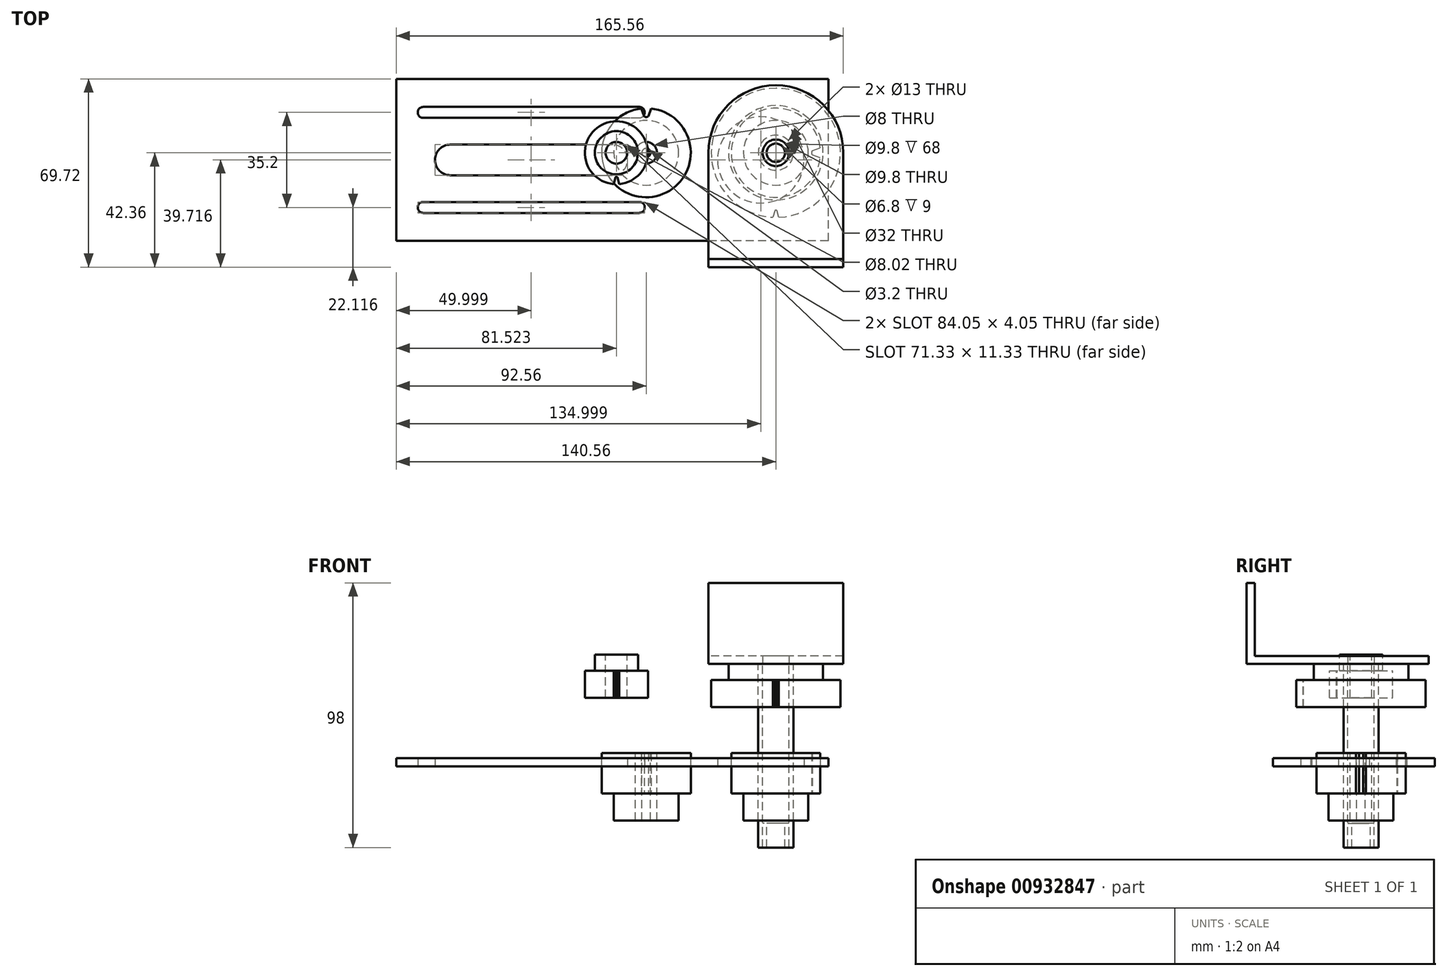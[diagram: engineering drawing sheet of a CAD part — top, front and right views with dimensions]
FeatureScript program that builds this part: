
annotation { "Feature Type Name" : "Feature", "Feature Type Description" : "" }
export const myFeature = defineFeature(function(context is Context, id is Id, definition is map)
    precondition{}
    {
        {
            var Q0;
            Q0=qCreatedBy(makeId("Front.planeOp"),FACE);
            var sketch = newSketch(context, id + "F0", { "sketchPlane" : qUnion([Q0])});
            skLineSegment(sketch, "E0", {"start": v(-76.12, 37.9) * mm, "end": v(-76.12, -21.1) * mm, "construction": true});
            skLineSegment(sketch, "E1", {"start": v(-76.12, -21.1) * mm, "end": v(-81.02, -21.1) * mm, "construction": true});
            skLineSegment(sketch, "E2", {"start": v(-81.02, -21.1) * mm, "end": v(-81.02, -30.1) * mm});
            skLineSegment(sketch, "E3", {"start": v(-81.02, -30.1) * mm, "end": v(-82.62, -30.1) * mm});
            skLineSegment(sketch, "E4", {"start": v(-82.62, -30.1) * mm, "end": v(-82.62, -20.1) * mm});
            skLineSegment(sketch, "E5", {"start": v(-82.62, -20.1) * mm, "end": v(-88.12, -20.1) * mm});
            skLineSegment(sketch, "E6", {"start": v(-88.12, -20.1) * mm, "end": v(-88.12, -10.1) * mm});
            skLineSegment(sketch, "E7", {"start": v(-82.62, -30.1) * mm, "end": v(-82.62, 31.9) * mm});
            skLineSegment(sketch, "E8", {"start": v(-100.04, 31.9) * mm, "end": v(-100.04, 21.9) * mm});
            skLineSegment(sketch, "E9", {"start": v(-139.17, 25.37) * mm, "end": v(-146.83, 25.37) * mm});
            skLineSegment(sketch, "E10", {"start": v(-146.83, 25.37) * mm, "end": v(-146.83, 35.37) * mm});
            skLineSegment(sketch, "E11", {"start": v(-81.02, -21.1) * mm, "end": v(-81.02, 37.9) * mm});
            skLineSegment(sketch, "E12", {"start": v(-81.02, -30.1) * mm, "end": v(-79.52, -30.1) * mm});
            skLineSegment(sketch, "E13", {"start": v(-79.52, -30.1) * mm, "end": v(-79.52, -21.1) * mm});
            skLineSegment(sketch, "E14", {"start": v(-79.52, -21.1) * mm, "end": v(-81.02, -21.1) * mm});
            skLineSegment(sketch, "E15", {"start": v(-82.62, -20.1) * mm, "end": v(-82.62, -30.1) * mm});
            skLineSegment(sketch, "E16", {"start": v(-92.62, -10.1) * mm, "end": v(-92.62, 4.9) * mm});
            skLineSegment(sketch, "E17", {"start": v(-92.62, 4.9) * mm, "end": v(-82.62, 4.9) * mm});
            skLineSegment(sketch, "E18", {"start": v(-124.12, 4.9) * mm, "end": v(-124.12, -20.1) * mm, "construction": true});
            skLineSegment(sketch, "E19", {"start": v(-128.12, -20.1) * mm, "end": v(-128.12, 4.9) * mm});
            skLineSegment(sketch, "E20", {"start": v(-128.12, 4.9) * mm, "end": v(-140.62, 4.9) * mm});
            skLineSegment(sketch, "E21", {"start": v(-140.62, 4.9) * mm, "end": v(-140.62, -10.1) * mm});
            skLineSegment(sketch, "E22", {"start": v(-140.62, -10.1) * mm, "end": v(-136.12, -10.1) * mm});
            skLineSegment(sketch, "E23", {"start": v(-136.12, -10.1) * mm, "end": v(-136.12, -20.1) * mm});
            skLineSegment(sketch, "E24", {"start": v(-136.12, -20.1) * mm, "end": v(-128.12, -20.1) * mm});
            skLineSegment(sketch, "E25", {"start": v(-88.12, -10.1) * mm, "end": v(-92.62, -10.1) * mm});
            skLineSegment(sketch, "E26", {"start": v(-128.12, -20.1) * mm, "end": v(-125.72, -20.1) * mm});
            skLineSegment(sketch, "E27", {"start": v(-125.72, -20.1) * mm, "end": v(-125.72, 4.9) * mm});
            skLineSegment(sketch, "E28", {"start": v(-125.72, -20.1) * mm, "end": v(-124.12, -20.1) * mm, "construction": true});
            skLineSegment(sketch, "E29", {"start": v(-128.12, 4.9) * mm, "end": v(-125.72, 4.9) * mm});
            skLineSegment(sketch, "E30", {"start": v(-125.72, 4.9) * mm, "end": v(-124.12, 4.9) * mm, "construction": true});
            skLineSegment(sketch, "E31", {"start": v(-100.04, 21.9) * mm, "end": v(-82.62, 21.9) * mm});
            skLineSegment(sketch, "E32", {"start": v(-82.62, 31.9) * mm, "end": v(-82.62, 37.9) * mm});
            skLineSegment(sketch, "E33", {"start": v(-82.62, 37.9) * mm, "end": v(-93.62, 37.9) * mm});
            skLineSegment(sketch, "E34", {"start": v(-93.62, 37.9) * mm, "end": v(-93.62, 31.9) * mm});
            skLineSegment(sketch, "E35", {"start": v(-93.62, 31.9) * mm, "end": v(-100.04, 31.9) * mm});
            skLineSegment(sketch, "E36", {"start": v(-139.17, 25.37) * mm, "end": v(-139.17, 41.37) * mm});
            skLineSegment(sketch, "E37", {"start": v(-139.17, 41.37) * mm, "end": v(-143.16, 41.37) * mm});
            skLineSegment(sketch, "E38", {"start": v(-143.16, 41.37) * mm, "end": v(-143.16, 35.37) * mm});
            skLineSegment(sketch, "E39", {"start": v(-146.83, 35.37) * mm, "end": v(-143.16, 35.37) * mm});
            skLineSegment(sketch, "E40", {"start": v(-139.17, 41.37) * mm, "end": v(-135.16, 41.37) * mm, "construction": true});
            skLineSegment(sketch, "E41", {"start": v(-135.16, 41.37) * mm, "end": v(-135.16, 25.37) * mm, "construction": true});
            skLineSegment(sketch, "E42", {"start": v(-135.16, 25.37) * mm, "end": v(-139.17, 25.37) * mm, "construction": true});
            skLineSegment(sketch, "E43", {"start": v(-82.62, 37.9) * mm, "end": v(-81.02, 37.9) * mm});
            skLineSegment(sketch, "E44", {"start": v(-81.02, 37.9) * mm, "end": v(-76.12, 37.9) * mm, "construction": true});
            skSolve(sketch);
        }
        {
            var Q0;
            Q0=qCreatedBy(makeId("Top.planeOp"),FACE);
            var sketch = newSketch(context, id + "F1", { "sketchPlane" : qUnion([Q0])});
            skLineSegment(sketch, "E45.bottom", {"start": v(-56.68, -32.64) * mm, "end": v(-216.68, -32.64) * mm});
            skLineSegment(sketch, "E45.top", {"start": v(-56.68, 27.36) * mm, "end": v(-216.68, 27.36) * mm});
            skLineSegment(sketch, "E45.left", {"start": v(-56.68, -32.64) * mm, "end": v(-56.68, 27.36) * mm});
            skLineSegment(sketch, "E45.right", {"start": v(-216.68, -32.64) * mm, "end": v(-216.68, 27.36) * mm});
            skLineSegment(sketch, "E46.bottom", {"start": v(-126.68, -22.27) * mm, "end": v(-206.68, -22.27) * mm});
            skLineSegment(sketch, "E46.top", {"start": v(-126.68, -18.22) * mm, "end": v(-206.68, -18.22) * mm});
            skLineSegment(sketch, "E46.left", {"start": v(-126.68, -22.27) * mm, "end": v(-126.68, -18.22) * mm});
            skLineSegment(sketch, "E46.right", {"start": v(-206.68, -22.27) * mm, "end": v(-206.68, -18.22) * mm});
            skLineSegment(sketch, "E47.bottom", {"start": v(-206.68, 16.98) * mm, "end": v(-126.68, 16.98) * mm});
            skLineSegment(sketch, "E47.top", {"start": v(-206.68, 12.93) * mm, "end": v(-126.68, 12.93) * mm});
            skLineSegment(sketch, "E47.left", {"start": v(-206.68, 16.98) * mm, "end": v(-206.68, 12.93) * mm});
            skLineSegment(sketch, "E47.right", {"start": v(-126.68, 16.98) * mm, "end": v(-126.68, 12.93) * mm});
            skLineSegment(sketch, "E48.bottom", {"start": v(-196.68, -8.3) * mm, "end": v(-136.68, -8.3) * mm});
            skLineSegment(sketch, "E48.top", {"start": v(-196.68, 3.02) * mm, "end": v(-136.68, 3.02) * mm});
            skLineSegment(sketch, "E48.left", {"start": v(-196.68, -8.3) * mm, "end": v(-196.68, 3.02) * mm});
            skLineSegment(sketch, "E48.right", {"start": v(-136.68, -8.3) * mm, "end": v(-136.68, 3.02) * mm});
            skCircle(sketch, "E49", {"center": v(-81.68, -2.64) * mm, "radius": 16 * mm});
            skLineSegment(sketch, "E50", {"start": v(-126.68, -22.27) * mm, "end": v(-126.68, -32.64) * mm, "construction": true});
            skLineSegment(sketch, "E51", {"start": v(-126.68, 16.98) * mm, "end": v(-126.68, 27.36) * mm, "construction": true});
            skLineSegment(sketch, "E52", {"start": v(-126.68, -18.22) * mm, "end": v(-126.68, 12.93) * mm, "construction": true});
            skLineSegment(sketch, "E53", {"start": v(-206.68, -18.22) * mm, "end": v(-206.68, 12.93) * mm, "construction": true});
            skLineSegment(sketch, "E54", {"start": v(-126.68, -2.64) * mm, "end": v(-136.68, -2.64) * mm, "construction": true});
            skLineSegment(sketch, "E55", {"start": v(-206.68, -2.64) * mm, "end": v(-196.68, -2.64) * mm, "construction": true});
            skLineSegment(sketch, "E56", {"start": v(-81.68, -32.64) * mm, "end": v(-81.68, 27.36) * mm, "construction": true});
            skArc(sketch, "E57", {"start": v(-126.68, 12.93) * mm, "mid": v(-124.66, 14.96) * mm, "end": v(-126.68, 16.98) * mm});
            skArc(sketch, "E58", {"start": v(-206.68, 16.98) * mm, "mid": v(-208.7, 14.96) * mm, "end": v(-206.68, 12.93) * mm});
            skArc(sketch, "E59", {"start": v(-126.68, -22.27) * mm, "mid": v(-124.66, -20.24) * mm, "end": v(-126.68, -18.22) * mm});
            skArc(sketch, "E60", {"start": v(-206.68, -18.22) * mm, "mid": v(-208.7, -20.24) * mm, "end": v(-206.68, -22.27) * mm});
            skArc(sketch, "E61", {"start": v(-136.68, -8.3) * mm, "mid": v(-131.02, -2.64) * mm, "end": v(-136.68, 3.02) * mm});
            skArc(sketch, "E62", {"start": v(-196.68, 3.02) * mm, "mid": v(-202.35, -2.64) * mm, "end": v(-196.68, -8.3) * mm});
            skSolve(sketch);
        }
        {
            var Q0;
            Q0=makeQuery(id+"F0.imprint","IMPRINT",FACE,{"disambiguationData":[TD([[makeQuery(id+"F0.imprint","IMPRINT",EDGE,{"derivedFrom":sQuery(id+"F0.wireOp",EDGE,"E2")}),-1.0]])]});
            var Q1;
            Q1=sQuery(id+"F0.wireOp",EDGE,"E0");
            revolve(context, id + "F2", {"surfaceOperationType" : NewSurfaceOperationType.NEW, "entities" : qUnion([Q0]), "axis" : qUnion([Q1]), "revolveType" : RevolveType.FULL});
        }
        {
            var Q0;
            Q0=makeQuery(id+"F0.imprint","IMPRINT",FACE,{"disambiguationData":[TD([[makeQuery(id+"F0.imprint","IMPRINT",EDGE,{"derivedFrom":sQuery(id+"F0.wireOp",EDGE,"E19")}),1.0]])]});
            var Q1;
            Q1=sQuery(id+"F0.wireOp",EDGE,"E18");
            revolve(context, id + "F3", {"surfaceOperationType" : NewSurfaceOperationType.NEW, "entities" : qUnion([Q0]), "axis" : qUnion([Q1]), "revolveType" : RevolveType.FULL});
        }
        {
            var Q0;
            Q0=makeQuery(id+"F0.imprint","IMPRINT",FACE,{"disambiguationData":[TD([[makeQuery(id+"F0.imprint","IMPRINT",EDGE,{"derivedFrom":sQuery(id+"F0.wireOp",EDGE,"E5")}),-1.0]])]});
            var Q1;
            Q1=sQuery(id+"F0.wireOp",EDGE,"E0");
            revolve(context, id + "F4", {"surfaceOperationType" : NewSurfaceOperationType.NEW, "entities" : qUnion([Q0]), "axis" : qUnion([Q1]), "revolveType" : RevolveType.FULL});
        }
        {
            var Q0;
            Q0=makeQuery(id+"F0.imprint","IMPRINT",FACE,{"disambiguationData":[TD([[makeQuery(id+"F0.imprint","IMPRINT",EDGE,{"derivedFrom":sQuery(id+"F0.wireOp",EDGE,"E8")}),1.0]])]});
            var Q1;
            Q1=sQuery(id+"F0.wireOp",EDGE,"E0");
            revolve(context, id + "F5", {"surfaceOperationType" : NewSurfaceOperationType.NEW, "entities" : qUnion([Q0]), "axis" : qUnion([Q1]), "revolveType" : RevolveType.FULL});
        }
        {
            var Q0;
            Q0=makeQuery(id+"F5.opRevolve","SWEPT_FACE",FACE,{"disambiguationData":[OSD([sQuery(id+"F0.wireOp",EDGE,"E35")])]});
            var sketch = newSketch(context, id + "F6", { "sketchPlane" : qUnion([Q0])});
            skCircle(sketch, "E63", {"center": v(-76.12, 0) * mm, "radius": 22.68 * mm, "construction": true});
            skCircle(sketch, "E64", {"center": v(-76.12, 0) * mm, "radius": 21.43 * mm, "construction": true});
            skLineSegment(sketch, "E65", {"start": v(-76.12, 0) * mm, "end": v(-76.12, -23.93) * mm, "construction": true});
            skLineSegment(sketch, "E66", {"start": v(-75.08, -23.9) * mm, "end": v(-75.74, -21.42) * mm});
            skLineSegment(sketch, "E67", {"start": v(-75.74, -21.42) * mm, "end": v(-76.5, -21.42) * mm, "construction": true});
            skLineSegment(sketch, "E68", {"start": v(-76.5, -21.42) * mm, "end": v(-77.16, -23.9) * mm});
            skArc(sketch, "E69", {"start": v(-75.74, -21.42) * mm, "mid": v(-76.12, -21.3) * mm, "end": v(-76.5, -21.42) * mm});
            skArc(sketch, "E70", {"start": v(-77.16, -23.9) * mm, "mid": v(-76.12, -23.92) * mm, "end": v(-75.08, -23.9) * mm});
            skSolve(sketch);
        }
        {
            var Q0;
            Q0=makeQuery(id+"F6.imprint","IMPRINT",FACE,{"disambiguationData":[TD([[makeQuery(id+"F6.imprint","IMPRINT",EDGE,{"derivedFrom":sQuery(id+"F6.wireOp",EDGE,"E66")}),1.0]])]});
            var Q1;
            Q1=makeQuery(id+"F5.opRevolve","SWEPT_FACE",FACE,{"disambiguationData":[OSD([sQuery(id+"F0.wireOp",EDGE,"E31")])]});
            extrude(context, id + "F7", {"entities" : qUnion([Q0]), "operationType" : NewBodyOperationType.REMOVE, "endBound" : BoundingType.UP_TO_SURFACE, "oppositeDirection" : true, "depth" : 25 * mm, "endBoundEntityFace" : qUnion([Q1]), "offsetDistance" : 25 * mm});
        }
        {
            var Q0;
            Q0=makeQuery(id+"F4.opRevolve","SWEPT_FACE",FACE,{"disambiguationData":[OSD([sQuery(id+"F0.wireOp",EDGE,"E25")])]});
            var sketch = newSketch(context, id + "F8", { "sketchPlane" : qUnion([Q0])});
            skCircle(sketch, "E71", {"center": v(-76.12, 0) * mm, "radius": 15 * mm, "construction": true});
            skCircle(sketch, "E72", {"center": v(-76.12, 0) * mm, "radius": 13.5 * mm, "construction": true});
            skLineSegment(sketch, "E73", {"start": v(-76.12, 0) * mm, "end": v(-59.63, 0) * mm, "construction": true});
            skLineSegment(sketch, "E74", {"start": v(-59.72, 1.81) * mm, "end": v(-62.64, 0.75) * mm});
            skLineSegment(sketch, "E75", {"start": v(-59.72, -1.81) * mm, "end": v(-62.64, -0.75) * mm});
            skLineSegment(sketch, "E76", {"start": v(-62.64, 0.75) * mm, "end": v(-62.64, -0.75) * mm});
            skArc(sketch, "E77", {"start": v(-59.72, -1.81) * mm, "mid": v(-59.63, 0) * mm, "end": v(-59.72, 1.81) * mm});
            skArc(sketch, "E78", {"start": v(-62.64, 0.75) * mm, "mid": v(-62.9, 0) * mm, "end": v(-62.64, -0.75) * mm});
            skSolve(sketch);
        }
        {
            var Q0;
            Q0=makeQuery(id+"F3.opRevolve","SWEPT_FACE",FACE,{"disambiguationData":[OSD([sQuery(id+"F0.wireOp",EDGE,"E22")])]});
            var sketch = newSketch(context, id + "F9", { "sketchPlane" : qUnion([Q0])});
            skCircle(sketch, "E79", {"center": v(-124.12, 0) * mm, "radius": 15 * mm, "construction": true});
            skCircle(sketch, "E80", {"center": v(-124.12, 0) * mm, "radius": 13.5 * mm, "construction": true});
            skLineSegment(sketch, "E81", {"start": v(-124.12, 0) * mm, "end": v(-124.12, -16.5) * mm});
            skLineSegment(sketch, "E82", {"start": v(-122.3, -16.4) * mm, "end": v(-123.37, -13.48) * mm});
            skLineSegment(sketch, "E83", {"start": v(-123.37, -13.48) * mm, "end": v(-124.87, -13.48) * mm, "construction": true});
            skLineSegment(sketch, "E84", {"start": v(-124.87, -13.48) * mm, "end": v(-125.93, -16.4) * mm});
            skArc(sketch, "E85", {"start": v(-123.37, -13.48) * mm, "mid": v(-124.12, -13.24) * mm, "end": v(-124.87, -13.48) * mm});
            skSolve(sketch);
        }
        {
            var Q0;
            Q0=makeQuery(id+"F0.imprint","IMPRINT",FACE,{"disambiguationData":[TD([[makeQuery(id+"F0.imprint","IMPRINT",EDGE,{"derivedFrom":sQuery(id+"F0.wireOp",EDGE,"E9")}),-1.0]])]});
            var Q1;
            Q1=sQuery(id+"F0.wireOp",EDGE,"E41");
            revolve(context, id + "F10", {"surfaceOperationType" : NewSurfaceOperationType.NEW, "entities" : qUnion([Q0]), "axis" : qUnion([Q1]), "revolveType" : RevolveType.FULL});
        }
        {
            var Q0;
            Q0=makeQuery(id+"F0.imprint","IMPRINT",FACE,{"disambiguationData":[TD([[makeQuery(id+"F0.imprint","IMPRINT",EDGE,{"derivedFrom":sQuery(id+"F0.wireOp",EDGE,"E2")}),1.0]])]});
            var Q1;
            Q1=sQuery(id+"F0.wireOp",EDGE,"E0");
            revolve(context, id + "F11", {"surfaceOperationType" : NewSurfaceOperationType.NEW, "entities" : qUnion([Q0]), "axis" : qUnion([Q1]), "revolveType" : RevolveType.FULL});
        }
        {
            var Q0;
            Q0=makeQuery(id+"F8.imprint","IMPRINT",FACE,{"disambiguationData":[TD([[makeQuery(id+"F8.imprint","IMPRINT",EDGE,{"derivedFrom":sQuery(id+"F8.wireOp",EDGE,"E74")}),1.0]])]});
            var Q1;
            Q1=makeQuery(id+"F8.imprint","IMPRINT",FACE,{"disambiguationData":[TD([[makeQuery(id+"F8.imprint","IMPRINT",EDGE,{"derivedFrom":sQuery(id+"F8.wireOp",EDGE,"E76")}),-1.0]])]});
            var Q2;
            {var subQ0=sQuery(id+"F8.wireOp",EDGE,"E77");Q2=makeQuery(id+"F8.imprint","IMPRINT",FACE,{"disambiguationData":[TD([[makeQuery(id+"F8.imprint","IMPRINT",EDGE,{"derivedFrom":subQ0}),-1.0]])]});}
            var Q3;
            Q3=makeQuery(id+"F4.opRevolve","SWEPT_FACE",FACE,{"disambiguationData":[OSD([sQuery(id+"F0.wireOp",EDGE,"E17")])]});
            extrude(context, id + "F12", {"entities" : qUnion([Q0, Q1, Q2]), "operationType" : NewBodyOperationType.REMOVE, "endBound" : BoundingType.UP_TO_SURFACE, "oppositeDirection" : true, "depth" : 25 * mm, "endBoundEntityFace" : qUnion([Q3]), "offsetDistance" : 25 * mm});
        }
        {
            var Q0;
            {var subQ5=sQuery(id+"F9.wireOp",EDGE,"E84");Q0=makeQuery(id+"F9.imprint","IMPRINT",FACE,{"disambiguationData":[TD([[makeQuery(id+"F9.imprint","IMPRINT",EDGE,{"derivedFrom":subQ5}),1.0]])]});}
            var Q1;
            {var subQ5=sQuery(id+"F9.wireOp",EDGE,"E82");Q1=makeQuery(id+"F9.imprint","IMPRINT",FACE,{"disambiguationData":[TD([[makeQuery(id+"F9.imprint","IMPRINT",EDGE,{"derivedFrom":subQ5}),1.0]])]});}
            var Q2;
            Q2=makeQuery(id+"F3.opRevolve","SWEPT_FACE",FACE,{"disambiguationData":[OSD([sQuery(id+"F0.wireOp",EDGE,"E20")])]});
            extrude(context, id + "F13", {"entities" : qUnion([Q0, Q1]), "operationType" : NewBodyOperationType.REMOVE, "endBound" : BoundingType.UP_TO_SURFACE, "oppositeDirection" : true, "depth" : 25 * mm, "endBoundEntityFace" : qUnion([Q2]), "offsetDistance" : 25 * mm});
        }
        {
            var Q0;
            Q0=makeQuery(id+"F0.imprint","IMPRINT",FACE,{"disambiguationData":[TD([[makeQuery(id+"F0.imprint","IMPRINT",EDGE,{"derivedFrom":sQuery(id+"F0.wireOp",EDGE,"E19")}),-1.0]])]});
            var Q1;
            Q1=sQuery(id+"F0.wireOp",EDGE,"E18");
            revolve(context, id + "F14", {"surfaceOperationType" : NewSurfaceOperationType.NEW, "entities" : qUnion([Q0]), "axis" : qUnion([Q1]), "revolveType" : RevolveType.FULL});
        }
        {
            var Q0;
            Q0=makeQuery(id+"F10.opRevolve","SWEPT_FACE",FACE,{"disambiguationData":[OSD([sQuery(id+"F0.wireOp",EDGE,"E39")])]});
            var sketch = newSketch(context, id + "F15", { "sketchPlane" : qUnion([Q0])});
            skCircle(sketch, "E86", {"center": v(-135.16, 0) * mm, "radius": 10.43 * mm, "construction": true});
            skCircle(sketch, "E87", {"center": v(-135.16, 0) * mm, "radius": 91.75 * mm, "construction": true});
            skLineSegment(sketch, "E88", {"start": v(-135.16, 0) * mm, "end": v(-135.16, -11.67) * mm, "construction": true});
            skCircle(sketch, "E89", {"center": v(-135.16, 0) * mm, "radius": 9.18 * mm, "construction": true});
            skLineSegment(sketch, "E90", {"start": v(-134.12, -11.63) * mm, "end": v(-134.78, -9.17) * mm});
            skLineSegment(sketch, "E91", {"start": v(-134.78, -9.17) * mm, "end": v(-135.53, -9.17) * mm, "construction": true});
            skLineSegment(sketch, "E92", {"start": v(-135.53, -9.17) * mm, "end": v(-136.2, -11.63) * mm});
            skArc(sketch, "E93", {"start": v(-136.2, -11.63) * mm, "mid": v(-135.16, -11.67) * mm, "end": v(-134.12, -11.63) * mm});
            skArc(sketch, "E94", {"start": v(-134.78, -9.17) * mm, "mid": v(-135.16, -8.91) * mm, "end": v(-135.53, -9.17) * mm});
            skSolve(sketch);
        }
        {
            var Q0;
            Q0=makeQuery(id+"F15.imprint","IMPRINT",FACE,{"disambiguationData":[TD([[makeQuery(id+"F15.imprint","IMPRINT",EDGE,{"derivedFrom":sQuery(id+"F15.wireOp",EDGE,"E90")}),1.0]])]});
            var Q1;
            Q1=makeQuery(id+"F10.opRevolve","SWEPT_FACE",FACE,{"disambiguationData":[OSD([sQuery(id+"F0.wireOp",EDGE,"E9")])]});
            extrude(context, id + "F16", {"entities" : qUnion([Q0]), "operationType" : NewBodyOperationType.REMOVE, "endBound" : BoundingType.UP_TO_SURFACE, "oppositeDirection" : true, "depth" : 25 * mm, "endBoundEntityFace" : qUnion([Q1]), "offsetDistance" : 25 * mm});
        }
        {
            var Q0;
            Q0=makeQuery(id+"F1.imprint","IMPRINT",FACE,{"disambiguationData":[TD([[makeQuery(id+"F1.imprint","IMPRINT",EDGE,{"derivedFrom":sQuery(id+"F1.wireOp",EDGE,"E45.bottom")}),-1.0]])]});
            extrude(context, id + "F17", {"entities" : qUnion([Q0]), "depth" : 3 * mm, "offsetDistance" : 25 * mm});
        }
        {
            var Q0;
            Q0=makeQuery(id+"F2.opRevolve","SWEPT_FACE",FACE,{"disambiguationData":[OSD([sQuery(id+"F0.wireOp",EDGE,"E43")])]});
            var sketch = newSketch(context, id + "F18", { "sketchPlane" : qUnion([Q0])});
            skCircle(sketch, "E95", {"center": v(-76.12, 0) * mm, "radius": 4.9 * mm});
            skLineSegment(sketch, "E96.bottom", {"start": v(-51.12, -42.36) * mm, "end": v(-101.12, -42.36) * mm});
            skLineSegment(sketch, "E96.top", {"start": v(-51.12, 0) * mm, "end": v(-101.12, 0) * mm, "construction": true});
            skLineSegment(sketch, "E96.left", {"start": v(-51.12, -42.36) * mm, "end": v(-51.12, 0) * mm});
            skLineSegment(sketch, "E96.right", {"start": v(-101.12, -42.36) * mm, "end": v(-101.12, 0) * mm});
            skArc(sketch, "E97", {"start": v(-51.12, 0) * mm, "mid": v(-76.12, 25) * mm, "end": v(-101.12, 0) * mm});
            skSolve(sketch);
        }
        {
            var Q0;
            Q0 = qSketchRegion(id + "F18", true);
            extrude(context, id + "F19", {"entities" : qUnion([Q0]), "depth" : 30 * mm, "offsetDistance" : 25 * mm});
        }
        {
            var Q0;
            Q0=makeQuery(id+"F19.opExtrude","SWEPT_FACE",FACE,{"disambiguationData":[OSD([sQuery(id+"F18.wireOp",EDGE,"E97")])]});
            var Q1;
            Q1=makeQuery(id+"F19.opExtrude","SWEPT_FACE",FACE,{"disambiguationData":[OSD([sQuery(id+"F18.wireOp",EDGE,"E95")])]});
            var Q2;
            Q2=makeQuery(id+"F19.opExtrude","CAP_FACE",FACE,{"disambiguationData":[OSD([sQuery(id+"F18.wireOp",EDGE,"E95"),sQuery(id+"F18.wireOp",EDGE,"E96.bottom"),sQuery(id+"F18.wireOp",EDGE,"E96.left"),sQuery(id+"F18.wireOp",EDGE,"E96.right"),sQuery(id+"F18.wireOp",EDGE,"E97")])],"isStart":false});
            var Q3;
            Q3=makeQuery(id+"F19.opExtrude","SWEPT_FACE",FACE,{"disambiguationData":[OSD([sQuery(id+"F18.wireOp",EDGE,"E96.left")])]});
            var Q4;
            Q4=makeQuery(id+"F19.opExtrude","SWEPT_FACE",FACE,{"disambiguationData":[OSD([sQuery(id+"F18.wireOp",EDGE,"E96.right")])]});
            shell(context, id + "F20", {"entities" : qUnion([Q0, Q1, Q2, Q3, Q4]), "thickness" : 3 * mm});
        }
    });
